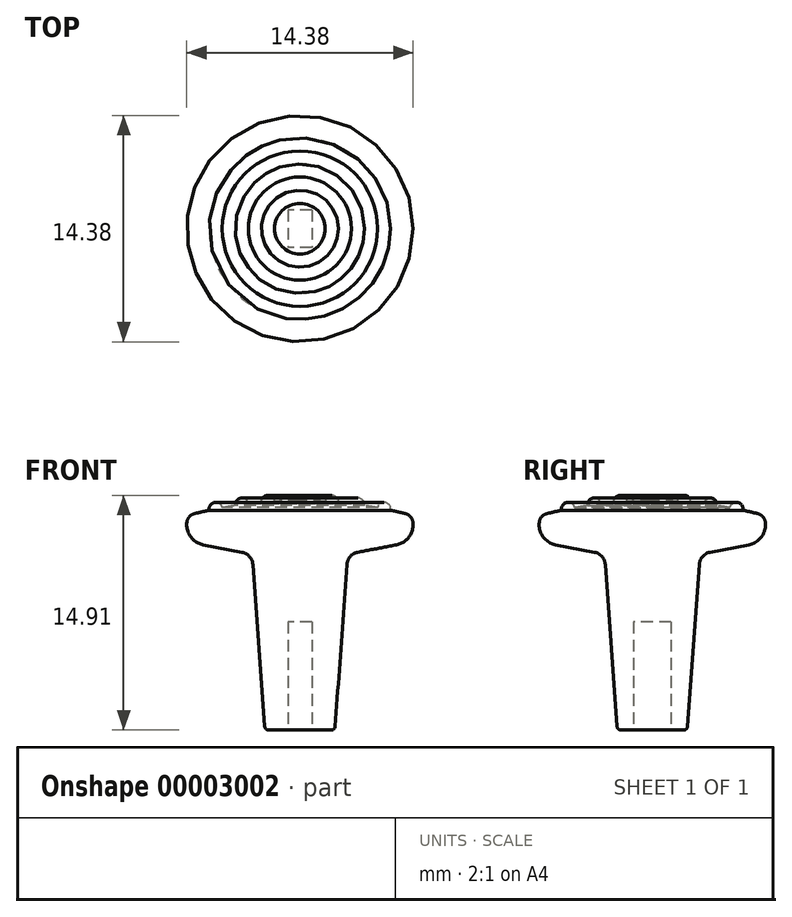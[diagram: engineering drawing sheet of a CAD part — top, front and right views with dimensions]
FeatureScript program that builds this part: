
annotation { "Feature Type Name" : "Feature", "Feature Type Description" : "" }
export const myFeature = defineFeature(function(context is Context, id is Id, definition is map)
    precondition{}
    {
        {
            var Q0;
            Q0=qCreatedBy(makeId("Right.planeOp"),FACE);
            var sketch = newSketch(context, id + "F0", { "sketchPlane" : qUnion([Q0])});
            skLineSegment(sketch, "E0", {"start": v(0, 0) * mm, "end": v(1.99, 0) * mm});
            skLineSegment(sketch, "E1", {"start": v(2.24, 0.24) * mm, "end": v(2.99, 10.52) * mm});
            skLineSegment(sketch, "E2", {"start": v(0, 13.04) * mm, "end": v(5.9, 13.04) * mm, "construction": true});
            skLineSegment(sketch, "E3", {"start": v(3.67, 11.3) * mm, "end": v(6.14, 11.77) * mm});
            skPoint(sketch, "E4", {"position": v(0, 14.99) * mm});
            skPoint(sketch, "E5.visualSharp", {"position": v(3.04, 11.17) * mm});
            skArc(sketch, "E5.filletArc", {"start": v(3.67, 11.3) * mm, "mid": v(3.2, 11.03) * mm, "end": v(2.99, 10.52) * mm});
            skArc(sketch, "E6", {"start": v(6.18, 14.3) * mm, "mid": v(3.1, 14.81) * mm, "end": v(0, 14.99) * mm, "construction": true});
            skLineSegment(sketch, "E7", {"start": v(0, 14.99) * mm, "end": v(7.18, 14.99) * mm, "construction": true});
            skArc(sketch, "E8", {"start": v(6.7, 13.75) * mm, "mid": v(6.23, 13.86) * mm, "end": v(5.76, 13.96) * mm});
            skArc(sketch, "E9", {"start": v(7.03, 13.66) * mm, "mid": v(4.72, 13.59) * mm, "end": v(6.14, 11.77) * mm, "construction": true});
            skArc(sketch, "E10", {"start": v(6.14, 11.77) * mm, "mid": v(6.95, 12.29) * mm, "end": v(7.18, 13.22) * mm});
            skPoint(sketch, "E11.visualSharp", {"position": v(7.03, 13.66) * mm});
            skArc(sketch, "E11.filletArc", {"start": v(7.18, 13.22) * mm, "mid": v(7.02, 13.56) * mm, "end": v(6.7, 13.75) * mm});
            skArc(sketch, "E12", {"start": v(2.44, 14.46) * mm, "mid": v(2.06, 14.91) * mm, "end": v(1.6, 14.52) * mm});
            skArc(sketch, "E13", {"start": v(4.1, 14.26) * mm, "mid": v(3.75, 14.74) * mm, "end": v(3.28, 14.37) * mm});
            skArc(sketch, "E14", {"start": v(5.76, 13.96) * mm, "mid": v(5.43, 14.46) * mm, "end": v(4.93, 14.13) * mm});
            skArc(sketch, "E15", {"start": v(1.6, 14.52) * mm, "mid": v(0.8, 14.56) * mm, "end": v(0, 14.57) * mm});
            skArc(sketch, "E16", {"start": v(2.44, 14.46) * mm, "mid": v(2.02, 14.5) * mm, "end": v(1.6, 14.52) * mm, "construction": true});
            skArc(sketch, "E17", {"start": v(3.28, 14.37) * mm, "mid": v(2.86, 14.42) * mm, "end": v(2.44, 14.46) * mm});
            skArc(sketch, "E18", {"start": v(4.1, 14.26) * mm, "mid": v(3.7, 14.32) * mm, "end": v(3.28, 14.37) * mm, "construction": true});
            skArc(sketch, "E19", {"start": v(4.93, 14.13) * mm, "mid": v(4.52, 14.2) * mm, "end": v(4.1, 14.26) * mm});
            skArc(sketch, "E20", {"start": v(5.76, 13.96) * mm, "mid": v(5.35, 14.05) * mm, "end": v(4.93, 14.13) * mm, "construction": true});
            skLineSegment(sketch, "E21", {"start": v(0, 14.57) * mm, "end": v(0, 0) * mm});
            skLineSegment(sketch, "E22", {"start": v(0, 14.99) * mm, "end": v(0, 22.08) * mm, "construction": true});
            skPoint(sketch, "E23.visualSharp", {"position": v(2.22, 0) * mm});
            skArc(sketch, "E23.filletArc", {"start": v(1.99, 0) * mm, "mid": v(2.16, 0.07) * mm, "end": v(2.24, 0.24) * mm});
            skSolve(sketch);
        }
        {
            var Q0;
            Q0=makeQuery(id+"F0.imprint","IMPRINT",FACE,{"disambiguationData":[TD([[makeQuery(id+"F0.imprint","IMPRINT",EDGE,{"derivedFrom":sQuery(id+"F0.wireOp",EDGE,"E0")}),1.0]])]});
            var Q1;
            Q1=sQuery(id+"F0.wireOp",EDGE,"E21");
            revolve(context, id + "F1", {"entities" : qUnion([Q0]), "axis" : qUnion([Q1]), "revolveType" : RevolveType.FULL});
        }
        {
            var Q0;
            Q0=makeQuery(id+"F1.opRevolve","SWEPT_FACE",FACE,{"disambiguationData":[OSD([sQuery(id+"F0.wireOp",EDGE,"E0")])]});
            var sketch = newSketch(context, id + "F2", { "sketchPlane" : qUnion([Q0])});
            skLineSegment(sketch, "E24.rect.bottom", {"start": v(0.76, -1.2) * mm, "end": v(-0.76, -1.2) * mm});
            skLineSegment(sketch, "E24.rect.top", {"start": v(0.76, 1.2) * mm, "end": v(-0.76, 1.2) * mm});
            skLineSegment(sketch, "E24.rect.left", {"start": v(0.76, -1.2) * mm, "end": v(0.76, 1.2) * mm});
            skLineSegment(sketch, "E24.rect.right", {"start": v(-0.76, -1.2) * mm, "end": v(-0.76, 1.2) * mm});
            skPoint(sketch, "E24.rect.middle", {"position": v(0, 0) * mm});
            skSolve(sketch);
        }
        {
            var Q0;
            Q0=makeQuery(id+"F2.imprint","IMPRINT",FACE,{"disambiguationData":[TD([[makeQuery(id+"F2.imprint","IMPRINT",EDGE,{"derivedFrom":sQuery(id+"F2.wireOp",EDGE,"E24.rect.bottom")}),-1.0]])]});
            extrude(context, id + "F3", {"entities" : qUnion([Q0]), "operationType" : NewBodyOperationType.REMOVE, "oppositeDirection" : true, "depth" : 6.88 * mm});
        }
    });
